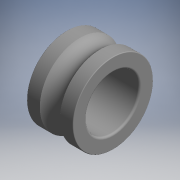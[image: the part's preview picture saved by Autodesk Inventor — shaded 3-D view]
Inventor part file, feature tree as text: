
AUTODESK INVENTOR PART (.ipt)
format: ipt  version: 2017.3 (Build 213256000, 256)  size: 150,528 bytes
history: native  units: mm (DEFAULTED — no unit token found)
features: revolve x1, sketch x1
ambient origin geometry x8: Origin, YZ Plane, XZ Plane, XY Plane, X Axis, Y Axis, Z Axis, Center Point
bodies: Solid1 (feature_tree)
feature tree (2):
  revolve  "Revolution1"  [1 undecoded]
  sketch  "Sketch_54"  dims[d0=360.0deg]
note: 1 required parameter value undecoded (feature->parameter linkage not recoverable at this tier; creation-order binding heuristic only, values carry confidence <= 0.55)
